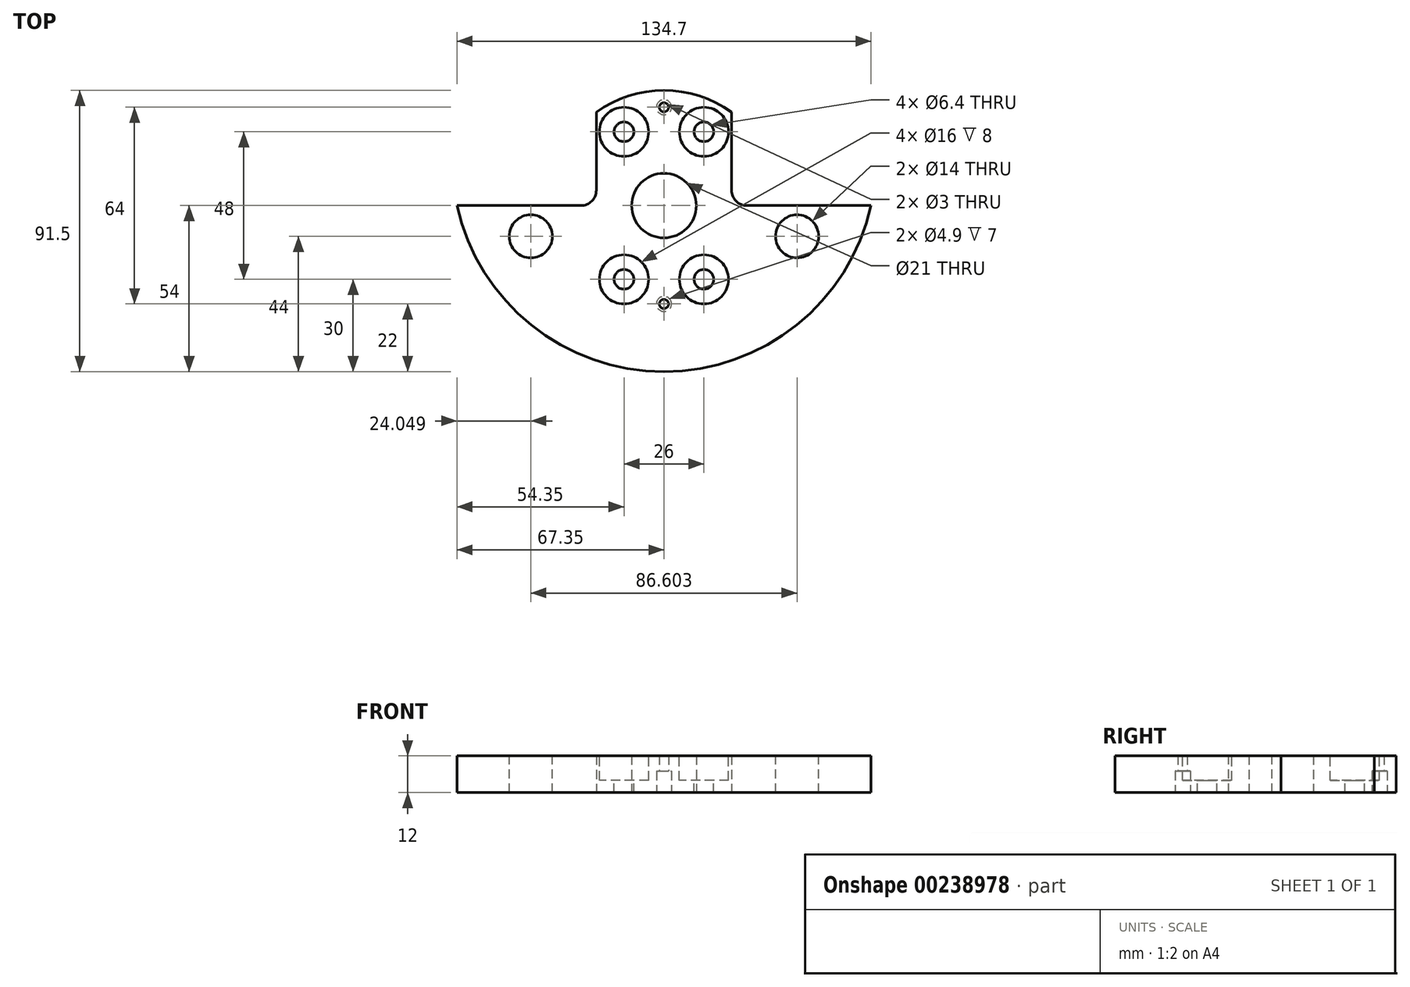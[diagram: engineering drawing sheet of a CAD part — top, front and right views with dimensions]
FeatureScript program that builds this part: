
annotation { "Feature Type Name" : "Feature", "Feature Type Description" : "" }
export const myFeature = defineFeature(function(context is Context, id is Id, definition is map)
    precondition{}
    {
        {
            var Q0;
            Q0=qCreatedBy(makeId("Top.planeOp"),FACE);
            cPlane(context, id + "F0", {"entities" : qUnion([Q0]), "cplaneType" : CPlaneType.OFFSET, "offset" : 19 * mm, "width" : 150 * mm, "height" : 150 * mm});
        }
        {
            var Q0;
            Q0=qCreatedBy(id+"F0.planeOp",FACE);
            var sketch = newSketch(context, id + "F1", { "sketchPlane" : qUnion([Q0])});
            skCircle(sketch, "E0.2", {"center": v(-13, -17) * mm, "radius": 2.26 * mm, "construction": true});
            skCircle(sketch, "E0.3", {"center": v(0, -28) * mm, "radius": 2.26 * mm, "construction": true});
            skLineSegment(sketch, "E1", {"start": v(-22, 30.37) * mm, "end": v(-22, 5) * mm});
            skCircle(sketch, "E2", {"center": v(0, 0) * mm, "radius": 10.5 * mm});
            skArc(sketch, "E3.trimOffspring", {"start": v(22, 30.37) * mm, "mid": v(0, 37.5) * mm, "end": v(-22, 30.37) * mm});
            skCircle(sketch, "E4.MirrorC", {"center": v(13, -17) * mm, "radius": 2.26 * mm, "construction": true});
            skCircle(sketch, "E5.MirrorC", {"center": v(-13, 17) * mm, "radius": 2.26 * mm, "construction": true});
            skCircle(sketch, "E6.MirrorC", {"center": v(13, 17) * mm, "radius": 2.26 * mm, "construction": true});
            skCircle(sketch, "E7.MirrorC", {"center": v(0, 28) * mm, "radius": 2.26 * mm, "construction": true});
            skPoint(sketch, "E8.visualSharp", {"position": v(-22, -3) * mm});
            skLineSegment(sketch, "E9.MirrorCS", {"start": v(22, 30.37) * mm, "end": v(22, 2) * mm});
            skPoint(sketch, "E10.orphan", {"position": v(22, -3) * mm});
            skArc(sketch, "E11.0", {"start": v(-67.35, 0) * mm, "mid": v(-43.16, -38.83) * mm, "end": v(0, -54) * mm});
            skPoint(sketch, "E12.orphan", {"position": v(-60.24, -3) * mm});
            skPoint(sketch, "E13.orphan", {"position": v(60.24, -3) * mm});
            skPoint(sketch, "E14", {"position": v(-121.76, 17) * mm});
            skLineSegment(sketch, "E15", {"start": v(-27, 0) * mm, "end": v(-68.2, 0) * mm});
            skPoint(sketch, "E16.newPointA", {"position": v(-16.57, 0) * mm});
            skPoint(sketch, "E16.newPointB", {"position": v(-22, 2) * mm});
            skArc(sketch, "E16.filletArc", {"start": v(-27, 0) * mm, "mid": v(-23.46, 1.46) * mm, "end": v(-22, 5) * mm});
            skLineSegment(sketch, "E17", {"start": v(0, 49.17) * mm, "end": v(0, -64.54) * mm, "construction": true});
            skPoint(sketch, "E17.startSnap0", {"position": v(0, 37.5) * mm});
            skArc(sketch, "E18.MirrorCS", {"start": v(27, 0) * mm, "mid": v(23.46, 1.46) * mm, "end": v(22, 5) * mm});
            skLineSegment(sketch, "E19.MirrorCS", {"start": v(27, 0) * mm, "end": v(68.2, 0) * mm});
            skArc(sketch, "E20.MirrorCS", {"start": v(67.35, 0) * mm, "mid": v(43.16, -38.83) * mm, "end": v(0, -54) * mm});
            skSolve(sketch);
        }
        {
            var Q0;
            Q0=qSketchRegion(id+"F1",true);
            extrude(context, id + "F2", {"entities" : qUnion([Q0]), "depth" : 12 * mm});
        }
        {
            var Q0;
            Q0=makeQuery(id+"F2.opExtrude","CAP_FACE",FACE,{"disambiguationData":[OSD([sQuery(id+"F1.wireOp",EDGE,"a7812266-889a-4506-a3f7-1cce787c8853.0.0"),sQuery(id+"F1.wireOp",EDGE,"E0.3"),sQuery(id+"F1.wireOp",EDGE,"E1"),sQuery(id+"F1.wireOp",EDGE,"E2"),sQuery(id+"F1.wireOp",EDGE,"99da5262-32bc-48f4-ae17-e0e4bb9571d20.MirrorCS"),sQuery(id+"F1.wireOp",EDGE,"E3.trimOffspring"),sQuery(id+"F1.wireOp",EDGE,"E7.MirrorC"),sQuery(id+"F1.wireOp",EDGE,"E8.filletArc"),sQuery(id+"F1.wireOp",EDGE,"adb206a8-7aa5-4657-84b1-35eb9b6c1d440.MirrorCS"),sQuery(id+"F1.wireOp",EDGE,"E9.MirrorCS"),sQuery(id+"F1.wireOp",EDGE,"E11.0")])],"isStart":false});
            cPlane(context, id + "F3", {"entities" : qUnion([Q0]), "cplaneType" : CPlaneType.OFFSET, "offset" : 0 * mm, "width" : 150 * mm, "height" : 150 * mm});
        }
        {
            var Q0;
            Q0=qCreatedBy(id+"F3.planeOp",FACE);
            var sketch = newSketch(context, id + "F4", { "sketchPlane" : qUnion([Q0])});
            skPoint(sketch, "E21.0", {"position": v(-13, -17) * mm});
            skPoint(sketch, "E22.0", {"position": v(13, -17) * mm});
            skPoint(sketch, "E23.0", {"position": v(-13, 17) * mm});
            skPoint(sketch, "E24.0", {"position": v(13, 17) * mm});
            skLineSegment(sketch, "E25", {"start": v(-4.37, -24) * mm, "end": v(-43.86, -24) * mm, "construction": true});
            skLineSegment(sketch, "E26", {"start": v(6.25, -32) * mm, "end": v(-31.83, -32) * mm, "construction": true});
            skLineSegment(sketch, "E27", {"start": v(-13, -7.18) * mm, "end": v(-13, -57.43) * mm, "construction": true});
            skPoint(sketch, "E28", {"position": v(-13, -24) * mm});
            skPoint(sketch, "E29", {"position": v(0, -32) * mm});
            skPoint(sketch, "E30.MirrorP", {"position": v(13, -24) * mm});
            skPoint(sketch, "E31.MirrorP", {"position": v(-13, 24) * mm});
            skPoint(sketch, "E32.MirrorP", {"position": v(0, 32) * mm});
            skPoint(sketch, "E33.MirrorP", {"position": v(13, 24) * mm});
            skSolve(sketch);
        }
        {
            var Q0;
            Q0=qCreatedBy(id+"F3.planeOp",FACE);
            var sketch = newSketch(context, id + "F5", { "sketchPlane" : qUnion([Q0])});
            skCircle(sketch, "E34", {"center": v(0, 0) * mm, "radius": 95 * mm, "construction": true});
            skPoint(sketch, "E35", {"position": v(-88.75, 30.02) * mm});
            skPoint(sketch, "E36", {"position": v(0, 15) * mm});
            skCircle(sketch, "E37", {"center": v(0, 15) * mm, "radius": 80 * mm, "construction": true});
            skCircle(sketch, "E38", {"center": v(0, 15) * mm, "radius": 70 * mm, "construction": true});
            skLineSegment(sketch, "E39", {"start": v(0, 15) * mm, "end": v(-99.15, 72.25) * mm, "construction": true});
            skLineSegment(sketch, "E40.MirrorCS", {"start": v(-88.75, 60.02) * mm, "end": v(10.4, 117.26) * mm, "construction": true});
            skArc(sketch, "E41.1.0", {"start": v(40.59, 44.2) * mm, "mid": v(7.54, 64.43) * mm, "end": v(-30.04, 54.97) * mm, "construction": true});
            skArc(sketch, "E42.trimOffspring", {"start": v(50.4, -7.04) * mm, "mid": v(47.63, 42.5) * mm, "end": v(6.11, 69.66) * mm});
            skArc(sketch, "E43.trimOffspring", {"start": v(-135.66, 77.32) * mm, "mid": v(-87, 10.05) * mm, "end": v(-43.17, 80.57) * mm, "construction": true});
            skCircle(sketch, "E44", {"center": v(0, 0) * mm, "radius": 15 * mm});
            skArc(sketch, "E45", {"start": v(-5, 65) * mm, "mid": v(0, 60) * mm, "end": v(5, 65) * mm});
            skLineSegment(sketch, "E46", {"start": v(5, 68.67) * mm, "end": v(5, 64.75) * mm});
            skLineSegment(sketch, "E47", {"start": v(-5, 68.67) * mm, "end": v(-5, 64.75) * mm});
            skArc(sketch, "E48.trimOffspring", {"start": v(-6.11, 69.66) * mm, "mid": v(-47.36, 42.97) * mm, "end": v(-50.82, -6.03) * mm});
            skLineSegment(sketch, "E49", {"start": v(-6.11, 69.66) * mm, "end": v(-5, 68.67) * mm});
            skLineSegment(sketch, "E50", {"start": v(6.11, 69.66) * mm, "end": v(5, 68.67) * mm});
            skCircle(sketch, "E51", {"center": v(0, 65) * mm, "radius": 5 * mm, "construction": true});
            skCircle(sketch, "E52", {"center": v(0, 65) * mm, "radius": 8.5 * mm, "construction": true});
            skCircle(sketch, "E53", {"center": v(0, 65) * mm, "radius": 20 * mm, "construction": true});
            skCircle(sketch, "E54.1.0", {"center": v(-43.3, -10) * mm, "radius": 8.5 * mm, "construction": true});
            skPoint(sketch, "E54.1.1", {"position": v(-43.3, -10) * mm});
            skCircle(sketch, "E54.1.2", {"center": v(-43.3, -10) * mm, "radius": 5 * mm, "construction": true});
            skLineSegment(sketch, "E54.1.3", {"start": v(-43.98, -16.16) * mm, "end": v(-40.58, -14.2) * mm});
            skArc(sketch, "E54.1.4", {"start": v(-40.8, -14.33) * mm, "mid": v(-38.97, -7.5) * mm, "end": v(-45.8, -5.67) * mm});
            skLineSegment(sketch, "E54.1.5", {"start": v(-44.28, -17.62) * mm, "end": v(-43.98, -16.16) * mm});
            skLineSegment(sketch, "E54.1.6", {"start": v(-48.98, -7.5) * mm, "end": v(-45.58, -5.54) * mm});
            skLineSegment(sketch, "E54.1.7", {"start": v(-50.4, -7.04) * mm, "end": v(-48.98, -7.5) * mm});
            skCircle(sketch, "E54.1.8", {"center": v(-43.3, -10) * mm, "radius": 20 * mm, "construction": true});
            skCircle(sketch, "E54.2.0", {"center": v(43.3, -10) * mm, "radius": 8.5 * mm, "construction": true});
            skPoint(sketch, "E54.2.1", {"position": v(43.3, -10) * mm});
            skCircle(sketch, "E54.2.2", {"center": v(43.3, -10) * mm, "radius": 5 * mm, "construction": true});
            skLineSegment(sketch, "E54.2.3", {"start": v(48.98, -7.5) * mm, "end": v(45.58, -5.54) * mm});
            skArc(sketch, "E54.2.4", {"start": v(45.8, -5.67) * mm, "mid": v(38.97, -7.5) * mm, "end": v(40.8, -14.33) * mm});
            skLineSegment(sketch, "E54.2.5", {"start": v(50.4, -7.04) * mm, "end": v(48.98, -7.5) * mm});
            skLineSegment(sketch, "E54.2.6", {"start": v(43.98, -16.16) * mm, "end": v(40.58, -14.2) * mm});
            skLineSegment(sketch, "E54.2.7", {"start": v(44.28, -17.62) * mm, "end": v(43.98, -16.16) * mm});
            skCircle(sketch, "E54.2.8", {"center": v(43.3, -10) * mm, "radius": 20 * mm, "construction": true});
            skArc(sketch, "E55.trimOffspring", {"start": v(-50.82, -6.03) * mm, "mid": v(-50.6, -6.54) * mm, "end": v(-50.4, -7.04) * mm});
            skArc(sketch, "E56.trimOffspring", {"start": v(-44.28, -17.62) * mm, "mid": v(0, -40) * mm, "end": v(44.28, -17.62) * mm});
            skCircle(sketch, "E57", {"center": v(0, 0) * mm, "radius": 55 * mm, "construction": true});
            skCircle(sketch, "E58", {"center": v(0, 0) * mm, "radius": 40 * mm, "construction": true});
            skCircle(sketch, "E59", {"center": v(0, 0) * mm, "radius": 33.5 * mm, "construction": true});
            skLineSegment(sketch, "E60", {"start": v(-103.75, 57.12) * mm, "end": v(-103.75, 8) * mm, "construction": true});
            skLineSegment(sketch, "E61", {"start": v(-119.99, 20.02) * mm, "end": v(-91.25, 20.02) * mm, "construction": true});
            skLineSegment(sketch, "E62", {"start": v(-119.99, 15.02) * mm, "end": v(-80, 15.02) * mm, "construction": true});
            skCircle(sketch, "E63", {"center": v(-103.75, 20.02) * mm, "radius": 3.2 * mm});
            skCircle(sketch, "E64", {"center": v(-88.75, 15.02) * mm, "radius": 2.5 * mm});
            skCircle(sketch, "E65.MirrorC", {"center": v(-73.75, 20.02) * mm, "radius": 3.2 * mm});
            skCircle(sketch, "E66.MirrorC", {"center": v(-103.75, 70.02) * mm, "radius": 3.2 * mm});
            skCircle(sketch, "E67.MirrorC", {"center": v(-73.75, 70.02) * mm, "radius": 3.2 * mm});
            skCircle(sketch, "E68.MirrorC", {"center": v(-88.75, 75.02) * mm, "radius": 2.5 * mm});
            skCircle(sketch, "E69", {"center": v(0, 0) * mm, "radius": 10.5 * mm, "construction": true});
            skSolve(sketch);
        }
        {
            var Q0;
            Q0=sQuery(id+"F4.wireOp",VERTEX,"E31.MirrorP");
            var Q1;
            Q1=sQuery(id+"F4.wireOp",VERTEX,"E33.MirrorP");
            var Q2;
            Q2=sQuery(id+"F4.wireOp",VERTEX,"E28");
            var Q3;
            Q3=sQuery(id+"F4.wireOp",VERTEX,"E30.MirrorP");
            var Q4;
            Q4=makeQuery(id+"F2.opExtrude","SWEPT_BODY",BODY,{"disambiguationData":[OSD([sQuery(id+"F1.wireOp",EDGE,"a7812266-889a-4506-a3f7-1cce787c8853.0.0"),sQuery(id+"F1.wireOp",EDGE,"E0.3"),sQuery(id+"F1.wireOp",EDGE,"E1"),sQuery(id+"F1.wireOp",EDGE,"E2"),sQuery(id+"F1.wireOp",EDGE,"99da5262-32bc-48f4-ae17-e0e4bb9571d20.MirrorCS"),sQuery(id+"F1.wireOp",EDGE,"E3.trimOffspring"),sQuery(id+"F1.wireOp",EDGE,"E7.MirrorC"),sQuery(id+"F1.wireOp",EDGE,"E8.filletArc"),sQuery(id+"F1.wireOp",EDGE,"adb206a8-7aa5-4657-84b1-35eb9b6c1d440.MirrorCS"),sQuery(id+"F1.wireOp",EDGE,"E9.MirrorCS"),sQuery(id+"F1.wireOp",EDGE,"E11.0")])]});
            hole(context, id + "F6", {"style" : HoleStyle.C_BORE, "endStyle" : HoleEndStyle.THROUGH, "holeDiameter" : 6.4 * mm, "cBoreDiameter" : 16 * mm, "cBoreDepth" : 8 * mm, "tappedDepth" : 12 * mm, "tapClearance" : 3, "startFromSketch" : true, "locations" : qUnion([Q0, Q1, Q2, Q3]), "scope" : qUnion([Q4])});
        }
        {
            var Q0;
            Q0=sQuery(id+"F5.wireOp",VERTEX,"E54.1.1");
            var Q1;
            Q1=sQuery(id+"F5.wireOp",VERTEX,"E54.2.1");
            var Q2;
            Q2=makeQuery(id+"F2.opExtrude","SWEPT_BODY",BODY,{"disambiguationData":[OSD([sQuery(id+"F1.wireOp",EDGE,"E1"),sQuery(id+"F1.wireOp",EDGE,"E2"),sQuery(id+"F1.wireOp",EDGE,"E3.trimOffspring"),sQuery(id+"F1.wireOp",EDGE,"E9.MirrorCS"),sQuery(id+"F1.wireOp",EDGE,"E11.0"),sQuery(id+"F1.wireOp",EDGE,"E15"),sQuery(id+"F1.wireOp",EDGE,"E16.filletArc"),sQuery(id+"F1.wireOp",EDGE,"E18.MirrorCS"),sQuery(id+"F1.wireOp",EDGE,"E19.MirrorCS"),sQuery(id+"F1.wireOp",EDGE,"E20.MirrorCS")])]});
            hole(context, id + "F7", {"style" : HoleStyle.SIMPLE, "endStyle" : HoleEndStyle.THROUGH, "holeDiameter" : 14 * mm, "tappedDepth" : 12 * mm, "tapClearance" : 3, "startFromSketch" : true, "locations" : qUnion([Q0, Q1]), "scope" : qUnion([Q2])});
        }
        {
            var Q0;
            Q0=makeQuery(id+"F2.opExtrude","CAP_FACE",FACE,{"disambiguationData":[OSD([sQuery(id+"F1.wireOp",EDGE,"E1"),sQuery(id+"F1.wireOp",EDGE,"E2"),sQuery(id+"F1.wireOp",EDGE,"E3.trimOffspring"),sQuery(id+"F1.wireOp",EDGE,"E9.MirrorCS"),sQuery(id+"F1.wireOp",EDGE,"E11.0"),sQuery(id+"F1.wireOp",EDGE,"E15"),sQuery(id+"F1.wireOp",EDGE,"E16.filletArc"),sQuery(id+"F1.wireOp",EDGE,"E18.MirrorCS"),sQuery(id+"F1.wireOp",EDGE,"E19.MirrorCS"),sQuery(id+"F1.wireOp",EDGE,"E20.MirrorCS")])],"isStart":true});
            var sketch = newSketch(context, id + "F8", { "sketchPlane" : qUnion([Q0])});
            skPoint(sketch, "E70.0", {"position": v(0, 32) * mm});
            skPoint(sketch, "E71.0", {"position": v(0, -32) * mm});
            skSolve(sketch);
        }
        {
            var Q0;
            Q0=sQuery(id+"F8.wireOp",VERTEX,"E70.0");
            var Q1;
            Q1=sQuery(id+"F8.wireOp",VERTEX,"E71.0");
            var Q2;
            Q2=makeQuery(id+"F2.opExtrude","SWEPT_BODY",BODY,{"disambiguationData":[OSD([sQuery(id+"F1.wireOp",EDGE,"E1"),sQuery(id+"F1.wireOp",EDGE,"E2"),sQuery(id+"F1.wireOp",EDGE,"E3.trimOffspring"),sQuery(id+"F1.wireOp",EDGE,"E9.MirrorCS"),sQuery(id+"F1.wireOp",EDGE,"E11.0"),sQuery(id+"F1.wireOp",EDGE,"E15"),sQuery(id+"F1.wireOp",EDGE,"E16.filletArc"),sQuery(id+"F1.wireOp",EDGE,"E18.MirrorCS"),sQuery(id+"F1.wireOp",EDGE,"E19.MirrorCS"),sQuery(id+"F1.wireOp",EDGE,"E20.MirrorCS")])]});
            hole(context, id + "F9", {"style" : HoleStyle.C_BORE, "endStyle" : HoleEndStyle.THROUGH, "holeDiameter" : 3 * mm, "cBoreDiameter" : 4.9 * mm, "cBoreDepth" : 7 * mm, "tappedDepth" : 12 * mm, "tapClearance" : 3, "startFromSketch" : true, "locations" : qUnion([Q0, Q1]), "scope" : qUnion([Q2])});
        }
    });
